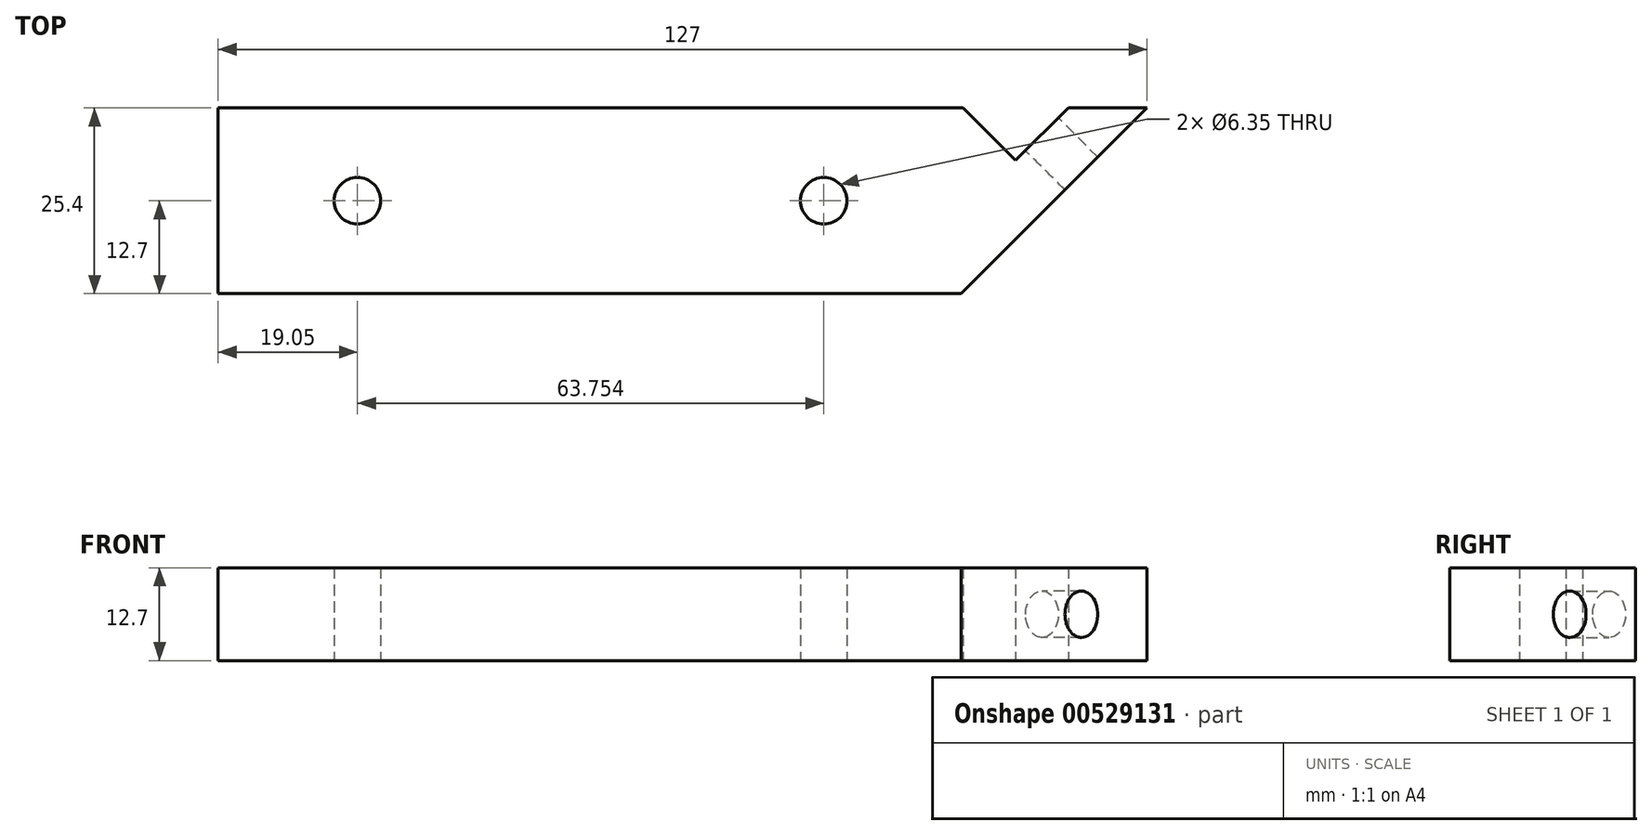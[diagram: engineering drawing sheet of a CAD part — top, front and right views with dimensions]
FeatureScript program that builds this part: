
annotation { "Feature Type Name" : "Feature", "Feature Type Description" : "" }
export const myFeature = defineFeature(function(context is Context, id is Id, definition is map)
    precondition{}
    {
        {
            var Q0;
            Q0=qCreatedBy(makeId("Top.planeOp"),FACE);
            var sketch = newSketch(context, id + "F0", { "sketchPlane" : qUnion([Q0])});
            skLineSegment(sketch, "E0.left", {"start": v(-63.5, 12.7) * mm, "end": v(-63.5, -12.7) * mm});
            skPoint(sketch, "E0.middle", {"position": v(0, 0) * mm});
            skLineSegment(sketch, "E1", {"start": v(-63.5, 0) * mm, "end": v(50.8, 0) * mm, "construction": true});
            skCircle(sketch, "E2", {"center": v(19.3, 0) * mm, "radius": 3.18 * mm});
            skCircle(sketch, "E3", {"center": v(-44.45, 0) * mm, "radius": 3.18 * mm});
            skLineSegment(sketch, "E4", {"start": v(63.5, 12.7) * mm, "end": v(38.1, -12.7) * mm, "construction": true});
            skLineSegment(sketch, "E5", {"start": v(-63.5, -12.7) * mm, "end": v(38.1, -12.7) * mm});
            skLineSegment(sketch, "E6", {"start": v(38.1, -12.7) * mm, "end": v(63.5, 12.7) * mm});
            skLineSegment(sketch, "E7", {"start": v(38.36, 12.7) * mm, "end": v(45.54, 5.52) * mm, "construction": true});
            skLineSegment(sketch, "E8", {"start": v(45.54, 5.52) * mm, "end": v(52.72, 12.7) * mm, "construction": true});
            skLineSegment(sketch, "E9", {"start": v(-63.5, 12.7) * mm, "end": v(38.36, 12.7) * mm});
            skLineSegment(sketch, "E10", {"start": v(45.54, 5.52) * mm, "end": v(38.36, 12.7) * mm});
            skLineSegment(sketch, "E11", {"start": v(45.54, 5.52) * mm, "end": v(52.72, 12.7) * mm});
            skLineSegment(sketch, "E12", {"start": v(52.72, 12.7) * mm, "end": v(63.5, 12.7) * mm});
            skSolve(sketch);
        }
        {
            var Q0;
            Q0 = qSketchRegion(id + "F0", true);
            extrude(context, id + "F1", {"entities" : qUnion([Q0]), "depth" : 12.7 * mm, "offsetDistance" : 25.4 * mm});
        }
        {
            var Q0;
            Q0=makeQuery(id+"F1.opExtrude","SWEPT_FACE",FACE,{"disambiguationData":[OSD([sQuery(id+"F0.wireOp",EDGE,"E11")])]});
            var sketch = newSketch(context, id + "F2", { "sketchPlane" : qUnion([Q0])});
            skLineSegment(sketch, "E13", {"start": v(-46.26, 6.35) * mm, "end": v(-36.1, 6.35) * mm, "construction": true});
            skLineSegment(sketch, "E14", {"start": v(-41.18, 12.7) * mm, "end": v(-41.18, 0) * mm, "construction": true});
            skCircle(sketch, "E15", {"center": v(-41.18, 6.35) * mm, "radius": 3.18 * mm});
            skSolve(sketch);
        }
        {
            var Q0;
            Q0 = qSketchRegion(id + "F2", true);
            extrude(context, id + "F3", {"entities" : qUnion([Q0]), "operationType" : NewBodyOperationType.REMOVE, "oppositeDirection" : true, "depth" : 16.79 * mm, "offsetDistance" : 25.4 * mm});
        }
    });
